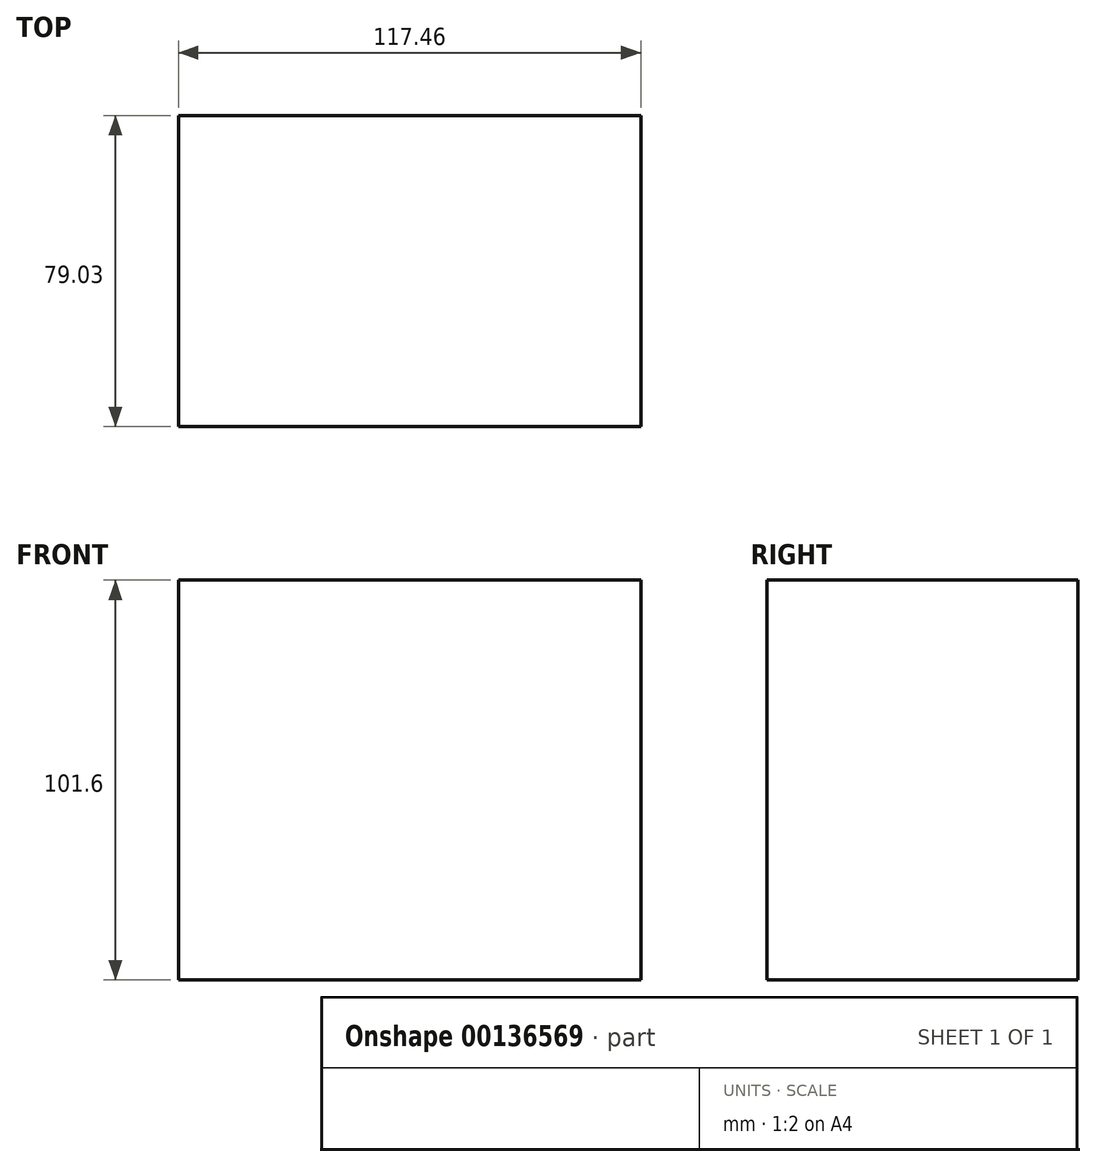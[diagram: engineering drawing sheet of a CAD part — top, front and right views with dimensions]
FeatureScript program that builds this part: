
annotation { "Feature Type Name" : "Feature", "Feature Type Description" : "" }
export const myFeature = defineFeature(function(context is Context, id is Id, definition is map)
    precondition{}
    {
        {
            var Q0;
            Q0=qCreatedBy(makeId("Top.planeOp"),FACE);
            var sketch = newSketch(context, id + "F0", { "sketchPlane" : qUnion([Q0])});
            skLineSegment(sketch, "E0.bottom", {"start": v(-54.41, 36.7) * mm, "end": v(63.05, 36.7) * mm});
            skLineSegment(sketch, "E0.top", {"start": v(-54.41, -42.32) * mm, "end": v(63.05, -42.32) * mm});
            skLineSegment(sketch, "E0.left", {"start": v(-54.41, 36.7) * mm, "end": v(-54.41, -42.32) * mm});
            skLineSegment(sketch, "E0.right", {"start": v(63.05, 36.7) * mm, "end": v(63.05, -42.32) * mm});
            skSolve(sketch);
        }
        {
            var Q0;
            Q0=makeQuery(id+"F0.imprint","IMPRINT",FACE,{"disambiguationData":[TD([[makeQuery(id+"F0.imprint","IMPRINT",EDGE,{"derivedFrom":sQuery(id+"F0.wireOp",EDGE,"E0.bottom")}),-1.0]])]});
            extrude(context, id + "F1", {"entities" : qUnion([Q0]), "depth" : 101.6 * mm});
        }
    });
